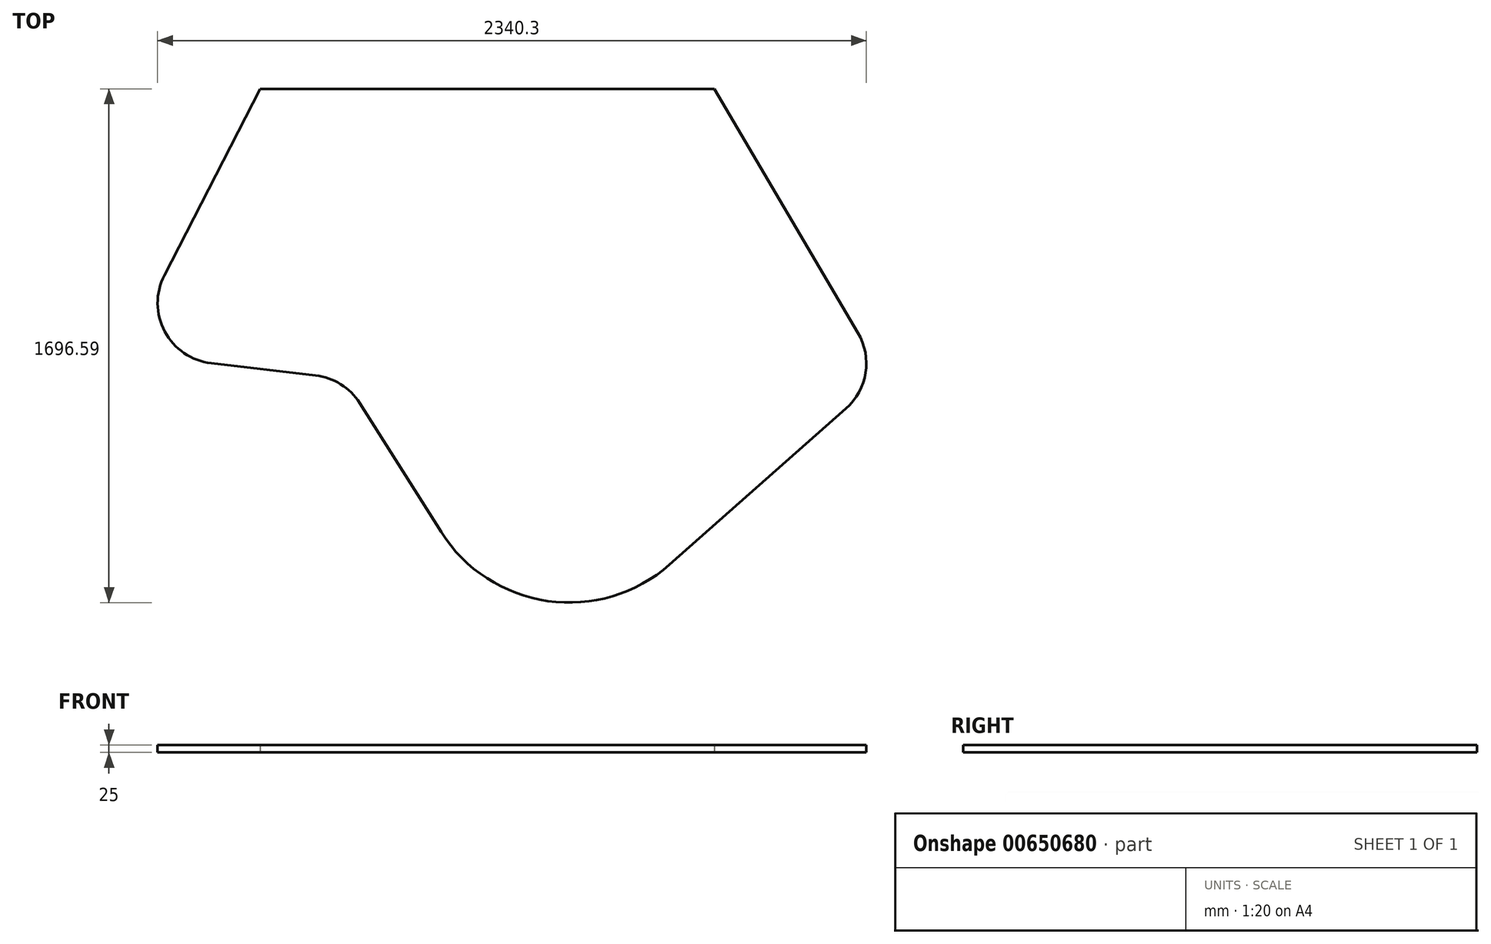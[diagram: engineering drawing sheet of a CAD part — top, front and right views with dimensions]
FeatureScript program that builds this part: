
annotation { "Feature Type Name" : "Feature", "Feature Type Description" : "" }
export const myFeature = defineFeature(function(context is Context, id is Id, definition is map)
    precondition{}
    {
        {
            var Q0;
            Q0=qCreatedBy(makeId("Top.planeOp"),FACE);
            var sketch = newSketch(context, id + "F0", { "sketchPlane" : qUnion([Q0])});
            skPoint(sketch, "E0.visualSharp", {"position": v(10767.76, 352.51) * mm});
            skLineSegment(sketch, "E1", {"start": v(8146.83, -957.73) * mm, "end": v(9646.83, -957.73) * mm});
            skLineSegment(sketch, "E2", {"start": v(8146.83, -957.73) * mm, "end": v(7830.55, -1573.73) * mm});
            skLineSegment(sketch, "E3", {"start": v(7985.37, -1863.74) * mm, "end": v(8329.68, -1903.78) * mm});
            skLineSegment(sketch, "E4", {"start": v(8475.62, -1995.55) * mm, "end": v(8745, -2421.55) * mm});
            skLineSegment(sketch, "E5", {"start": v(9498.73, -2528.95) * mm, "end": v(10081.22, -2014.1) * mm});
            skLineSegment(sketch, "E6", {"start": v(10121.09, -1762.73) * mm, "end": v(9646.83, -957.73) * mm});
            skPoint(sketch, "E7.visualSharp", {"position": v(9058.8, -2917.8) * mm});
            skArc(sketch, "E7.filletArc", {"start": v(8745, -2421.55) * mm, "mid": v(9097.06, -2649.32) * mm, "end": v(9498.73, -2528.95) * mm});
            skPoint(sketch, "E8.visualSharp", {"position": v(8424.56, -1914.81) * mm});
            skArc(sketch, "E8.filletArc", {"start": v(8475.62, -1995.55) * mm, "mid": v(8413.04, -1933.13) * mm, "end": v(8329.68, -1903.78) * mm});
            skPoint(sketch, "E9.visualSharp", {"position": v(10204.82, -1904.86) * mm});
            skArc(sketch, "E9.filletArc", {"start": v(10081.22, -2014.1) * mm, "mid": v(10146.3, -1895.58) * mm, "end": v(10121.09, -1762.73) * mm});
            skPoint(sketch, "E10.visualSharp", {"position": v(7698.77, -1830.4) * mm});
            skArc(sketch, "E10.filletArc", {"start": v(7830.55, -1573.73) * mm, "mid": v(7832.04, -1759.26) * mm, "end": v(7985.37, -1863.74) * mm});
            skSolve(sketch);
        }
        {
            var Q0;
            Q0 = qSketchRegion(id + "F0", true);
            var Q1;
            Q1=makeQuery(id+"F0.imprint","IMPRINT",FACE,{"disambiguationData":[TD([[makeQuery(id+"F0.imprint","IMPRINT",EDGE,{"derivedFrom":sQuery(id+"F0.wireOp",EDGE,"CtnbfG2p-W4To-eKo9-zetS-6qiDjGUlMzR9")}),1.0]])]});
            extrude(context, id + "F1", {"entities" : qUnion([Q0, Q1]), "depth" : 1 * mm, "offsetDistance" : 25 * mm});
        }
        {
            var Q0;
            Q0 = qSketchRegion(id + "F0", true);
            extrude(context, id + "F2", {"entities" : qUnion([Q0]), "operationType" : NewBodyOperationType.ADD, "depth" : 25 * mm, "offsetDistance" : 25 * mm});
        }
    });
